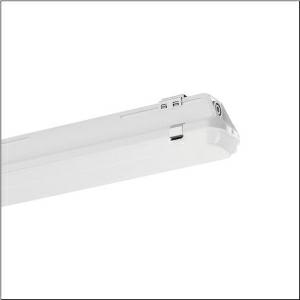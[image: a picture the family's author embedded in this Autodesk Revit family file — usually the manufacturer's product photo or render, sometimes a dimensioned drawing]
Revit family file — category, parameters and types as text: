
# Revit family: monsun_r__21_51fb207p430j_73f4
name_source: partatom
category: Lighting Fixtures
units: mm (PartAtom-declared; Revit-internal decimal feet)

## family parameters
Cut with Voids When Loaded = No
Host = Face
Light Source = No
Part Type = Normal
Room Calculation Point = No
Round Connector Dimension = Use Diameter
Shared = No

## types (1)
- Monsun® 21 (1 x LED, 3340 lm, 22.2 W, 4000K)
    Apparent Load = 22 VA
    CIE Flux Codes = 45 75 93 94 100
    Color Rendering = 80
    Color Temperature = 4000K
    Default Elevation = 1800 mm
    Description = Monsun® 21, damp-proof luminaire, chain hanger, primary optical cover: enclosure, of PC, light emission: direct distribution, primary light characteristic: symmetric, installation type: suspended mounting, surface-mounted, horizontal mounting, vertical mounting, LED, rated luminous flux: 3.340lm, luminous efficacy: 150lm/W, light colour: 840, colour temperature: 4000K, control gear: ECG, with terminal, 3-pole, max. 2.5mm², mains connection: 220..240V, AC, 50/60Hz, rated input power: 22W, housing, of glass-fibre reinforced polyester, uncoated, bright grey, length: 1.590mm, width: 90mm, height: 88mm, clip for enclosure, of stainless steel (V2A), ceiling mounting element, of stainless steel (V2A), chain hanger, of stainless steel (V2A), protection rating (complete): IP66, insulation class (complete): insulation class I (protective earthing), certification: CE, ENEC, VDE, UKCA, protection symbol: D, impact resistance: IK08, permissible operating ambient temperature: -25..+35°C, standard: EN 50419, EN 60598-2-1, corresponds to IFS (International Featured Standards) requirements for safety and quality in the food industry, for indoor or canopied outdoor use, no direct snow, no direct sun, no direct rain, packaging unit: 1 piece
    Height = 89 mm
    Lamp = 1 x LED
    Lamp Light Flux = 3340 lm
    Lamp Power = 22.2 W
    Lamp count = 1
    Length = 1590 mm
    Luminous efficacy = 150 lm/W
    Manufacturer = Siteco
    ModVariant = No
    Model = 51FB207P430J
    Mounting Place = Ceiling
    Mounting Type = Pendant
    Number of Poles = 1
    OnlyDefault = Yes
    Power Factor = 1
    Product Name = Monsun® 21
    Product group = damp-proof luminaire | ceiling pendant
    ProductGroupID = 908
    Protection Class = Protection class I
    Protection Degree = IP 66
    RLX_Detail_Level = 1
    RlxData = <blob elided: 88389 chars, md5=867c5dca>
    Socket = socket
    Standby Power = 0 W
    System Light Flux = 3340 lm
    System Power = 22 W
    Type Comments = Product without accessories
    Type Image = l_1006717.jpg
    URL = http://relux.com
    VarID = ---
    Voltage = 0 V
    Weight = 0.00 kg
    Width = 90 mm

## geometry (parser evidence)
native form markers: Blend x4, Sweep x15
no freeform markers — native parametric forms only
